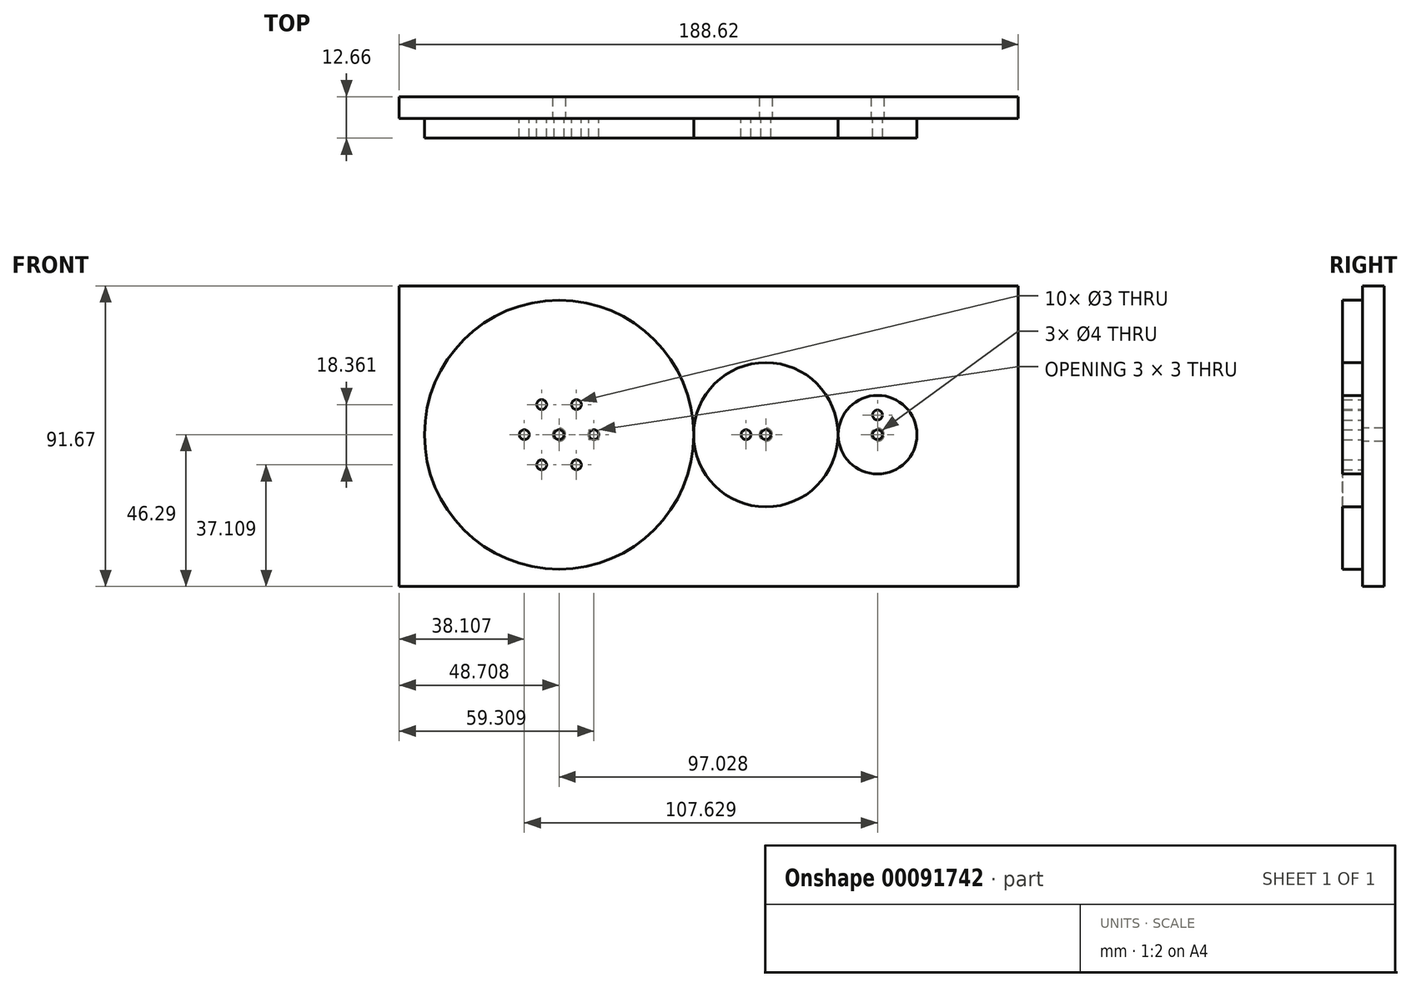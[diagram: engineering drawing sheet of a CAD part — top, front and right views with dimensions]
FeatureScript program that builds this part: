
annotation { "Feature Type Name" : "Feature", "Feature Type Description" : "" }
export const myFeature = defineFeature(function(context is Context, id is Id, definition is map)
    precondition{}
    {
        {
            var Q0;
            Q0=qCreatedBy(makeId("Front.planeOp"),FACE);
            var sketch = newSketch(context, id + "F0", { "sketchPlane" : qUnion([Q0])});
            skCircle(sketch, "E0", {"center": v(0, 0) * mm, "radius": 22 * mm});
            skCircle(sketch, "E1", {"center": v(34.04, 0) * mm, "radius": 11.99 * mm});
            skCircle(sketch, "E2", {"center": v(-63, 0) * mm, "radius": 41 * mm});
            skCircle(sketch, "E3", {"center": v(-63, 0) * mm, "radius": 1.5 * mm});
            skCircle(sketch, "E4", {"center": v(0, 0) * mm, "radius": 1.5 * mm});
            skCircle(sketch, "E5", {"center": v(34.04, 0) * mm, "radius": 1.5 * mm});
            skCircle(sketch, "E6", {"center": v(-73.6, 0) * mm, "radius": 1.5 * mm});
            skCircle(sketch, "E7.1.0", {"center": v(-68.3, 9.18) * mm, "radius": 1.5 * mm});
            skCircle(sketch, "E7.2.0", {"center": v(-57.7, 9.18) * mm, "radius": 1.5 * mm});
            skCircle(sketch, "E7.3.0", {"center": v(-52.4, 0) * mm, "radius": 1.5 * mm});
            skCircle(sketch, "E7.4.0", {"center": v(-57.7, -9.18) * mm, "radius": 1.5 * mm});
            skCircle(sketch, "E7.5.0", {"center": v(-68.3, -9.18) * mm, "radius": 1.5 * mm});
            skLineSegment(sketch, "E7.anchor1", {"start": v(-63, 0) * mm, "end": v(-73.6, 0) * mm, "construction": true});
            skLineSegment(sketch, "E7.anchor2", {"start": v(-63, 0) * mm, "end": v(-68.3, -9.18) * mm, "construction": true});
            skCircle(sketch, "E8", {"center": v(-6.04, 0) * mm, "radius": 1.5 * mm});
            skCircle(sketch, "E9.1.0", {"center": v(-0.05, -40.08) * mm, "radius": 1.5 * mm});
            skCircle(sketch, "E9.2.0", {"center": v(40.03, -34.08) * mm, "radius": 1.5 * mm});
            skCircle(sketch, "E9.3.0", {"center": v(34.04, 6) * mm, "radius": 1.5 * mm});
            skPoint(sketch, "E9.center", {"position": v(17, -17.04) * mm});
            skLineSegment(sketch, "E10", {"start": v(-63, 0) * mm, "end": v(0, 0) * mm, "construction": true});
            skLineSegment(sketch, "E11", {"start": v(-63, 0) * mm, "end": v(-94.77, 25.9) * mm, "construction": true});
            skLineSegment(sketch, "E12", {"start": v(0, 0) * mm, "end": v(12.15, -18.34) * mm, "construction": true});
            skLineSegment(sketch, "E13", {"start": v(34.04, 0) * mm, "end": v(45.85, -2.04) * mm, "construction": true});
            skLineSegment(sketch, "E14", {"start": v(34.04, 0) * mm, "end": v(34.04, -11.99) * mm, "construction": true});
            skLineSegment(sketch, "E15", {"start": v(-63, 0) * mm, "end": v(-63, -41) * mm, "construction": true});
            skLineSegment(sketch, "E16", {"start": v(-63, -41) * mm, "end": v(34.04, -11.99) * mm, "construction": true});
            skLineSegment(sketch, "E17", {"start": v(0, 0) * mm, "end": v(34.04, 0) * mm});
            skLineSegment(sketch, "E18", {"start": v(-63, 0) * mm, "end": v(34.04, 0) * mm});
            skLineSegment(sketch, "E19", {"start": v(34.04, 0) * mm, "end": v(34.04, 11.99) * mm, "construction": true});
            skLineSegment(sketch, "E20.bottom", {"start": v(215.9, 279.4) * mm, "end": v(-215.9, 279.4) * mm});
            skLineSegment(sketch, "E20.top", {"start": v(215.9, -279.4) * mm, "end": v(-215.9, -279.4) * mm});
            skLineSegment(sketch, "E20.left", {"start": v(215.9, 279.4) * mm, "end": v(215.9, -279.4) * mm});
            skLineSegment(sketch, "E20.right", {"start": v(-215.9, 279.4) * mm, "end": v(-215.9, -279.4) * mm});
            skSolve(sketch);
        }
        {
            var Q0;
            Q0=makeQuery(id+"F0.imprint","IMPRINT",FACE,{"disambiguationData":[TD([[makeQuery(id+"F0.imprint","IMPRINT",EDGE,{"derivedFrom":sQuery(id+"F0.wireOp",EDGE,"E2")}),1.0]])]});
            var Q1;
            Q1=makeQuery(id+"F0.imprint","IMPRINT",FACE,{"disambiguationData":[TD([[makeQuery(id+"F0.imprint","IMPRINT",EDGE,{"derivedFrom":sQuery(id+"F0.wireOp",EDGE,"E0")}),1.0]])]});
            var Q2;
            Q2=makeQuery(id+"F0.imprint","IMPRINT",FACE,{"disambiguationData":[TD([[makeQuery(id+"F0.imprint","IMPRINT",EDGE,{"derivedFrom":sQuery(id+"F0.wireOp",EDGE,"E1")}),1.0]])]});
            var Q3;
            Q3=makeQuery(id+"F0.imprint","IMPRINT",FACE,{"disambiguationData":[TD([[makeQuery(id+"F0.imprint","IMPRINT",EDGE,{"derivedFrom":sQuery(id+"F0.wireOp",EDGE,"E5")}),-1.0]])]});
            extrude(context, id + "F1", {"entities" : qUnion([Q0, Q1, Q2, Q3]), "depth" : 6 * mm});
        }
        {
            var Q0;
            Q0=qCreatedBy(makeId("Front.planeOp"),FACE);
            var sketch = newSketch(context, id + "F2", { "sketchPlane" : qUnion([Q0])});
            skCircle(sketch, "E21", {"center": v(0, 0) * mm, "radius": 22 * mm, "construction": true});
            skLineSegment(sketch, "E22", {"start": v(0, 0) * mm, "end": v(-15.05, 16.04) * mm, "construction": true});
            skLineSegment(sketch, "E23", {"start": v(0, 0) * mm, "end": v(-63, 0) * mm, "construction": true});
            skLineSegment(sketch, "E24.bottom", {"start": v(-111.7, 45.38) * mm, "end": v(76.92, 45.38) * mm});
            skLineSegment(sketch, "E24.top", {"start": v(-111.7, -46.3) * mm, "end": v(76.92, -46.3) * mm});
            skLineSegment(sketch, "E24.left", {"start": v(-111.7, 45.38) * mm, "end": v(-111.7, -46.3) * mm});
            skLineSegment(sketch, "E24.right", {"start": v(76.92, 45.38) * mm, "end": v(76.92, -46.3) * mm});
            skLineSegment(sketch, "E25", {"start": v(0, 0) * mm, "end": v(-63, 0) * mm});
            skLineSegment(sketch, "E26", {"start": v(0, 0) * mm, "end": v(34.04, 0) * mm});
            skCircle(sketch, "E27", {"center": v(-63, 0) * mm, "radius": 2 * mm});
            skLineSegment(sketch, "E28", {"start": v(-63, 0) * mm, "end": v(-61.58, 1.41) * mm});
            skCircle(sketch, "E29", {"center": v(0, 0) * mm, "radius": 2 * mm});
            skCircle(sketch, "E30", {"center": v(34.04, 0) * mm, "radius": 2 * mm});
            skLineSegment(sketch, "E31", {"start": v(0, 0) * mm, "end": v(1.46, 1.37) * mm});
            skLineSegment(sketch, "E32", {"start": v(34.04, 0) * mm, "end": v(35.56, 1.3) * mm});
            skSolve(sketch);
        }
        {
            var Q0;
            Q0 = qSketchRegion(id + "F2", true);
            extrude(context, id + "F3", {"entities" : qUnion([Q0]), "oppositeDirection" : true, "depth" : 6.66 * mm});
        }
    });
